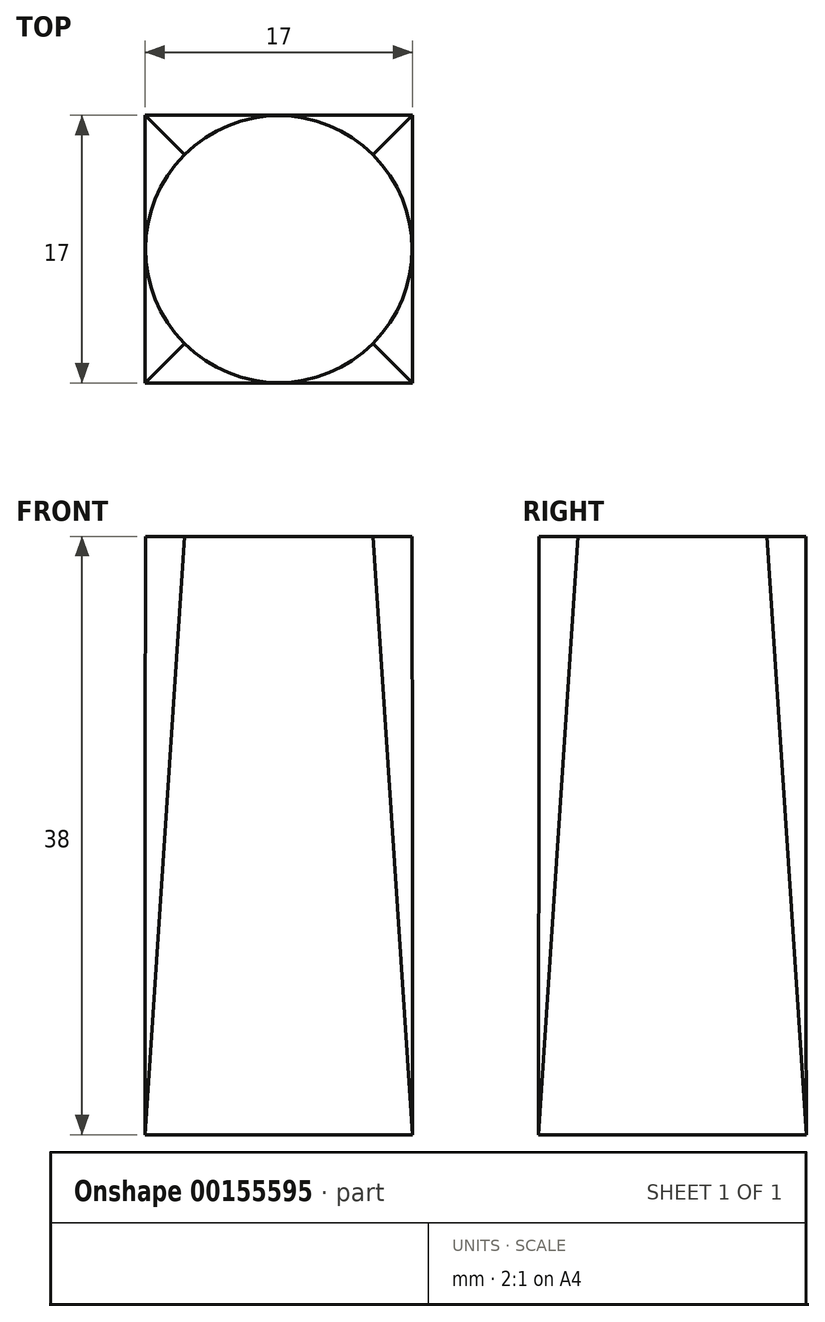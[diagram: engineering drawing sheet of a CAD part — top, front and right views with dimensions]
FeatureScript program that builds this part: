
annotation { "Feature Type Name" : "Feature", "Feature Type Description" : "" }
export const myFeature = defineFeature(function(context is Context, id is Id, definition is map)
    precondition{}
    {
        {
            var Q0;
            Q0=qCreatedBy(makeId("Top.planeOp"),FACE);
            var sketch = newSketch(context, id + "F0", { "sketchPlane" : qUnion([Q0])});
            skLineSegment(sketch, "E0.bottom", {"start": v(8.5, 8.5) * mm, "end": v(-8.5, 8.5) * mm});
            skLineSegment(sketch, "E0.top", {"start": v(8.5, -8.5) * mm, "end": v(-8.5, -8.5) * mm});
            skLineSegment(sketch, "E0.left", {"start": v(8.5, 8.5) * mm, "end": v(8.5, -8.5) * mm});
            skLineSegment(sketch, "E0.right", {"start": v(-8.5, 8.5) * mm, "end": v(-8.5, -8.5) * mm});
            skPoint(sketch, "E0.middle", {"position": v(0, 0) * mm});
            skSolve(sketch);
        }
        {
            var Q0;
            Q0=qCreatedBy(makeId("Top.planeOp"),FACE);
            cPlane(context, id + "F1", {"entities" : qUnion([Q0]), "cplaneType" : CPlaneType.OFFSET, "offset" : 38 * mm, "width" : 150 * mm, "height" : 150 * mm});
        }
        {
            var Q0;
            Q0=qCreatedBy(id+"F1.planeOp",FACE);
            var sketch = newSketch(context, id + "F2", { "sketchPlane" : qUnion([Q0])});
            skCircle(sketch, "E1", {"center": v(0, 0) * mm, "radius": 8.47 * mm});
            skSolve(sketch);
        }
        {
            var Q0;
            Q0=makeQuery(id+"F0.imprint","IMPRINT",FACE,{"disambiguationData":[TD([[makeQuery(id+"F0.imprint","IMPRINT",EDGE,{"derivedFrom":sQuery(id+"F0.wireOp",EDGE,"E0.bottom")}),1.0]])]});
            var Q1;
            Q1=makeQuery(id+"F2.imprint","IMPRINT",FACE,{"disambiguationData":[TD([[makeQuery(id+"F2.imprint","IMPRINT",EDGE,{"derivedFrom":sQuery(id+"F2.wireOp",EDGE,"E1")}),1.0]])]});
            loft(context, id + "F3", {"sheetProfilesArray" : [{ "sheetProfileEntities" : qUnion([Q0]) }, { "sheetProfileEntities" : qUnion([Q1]) }]});
        }
    });
